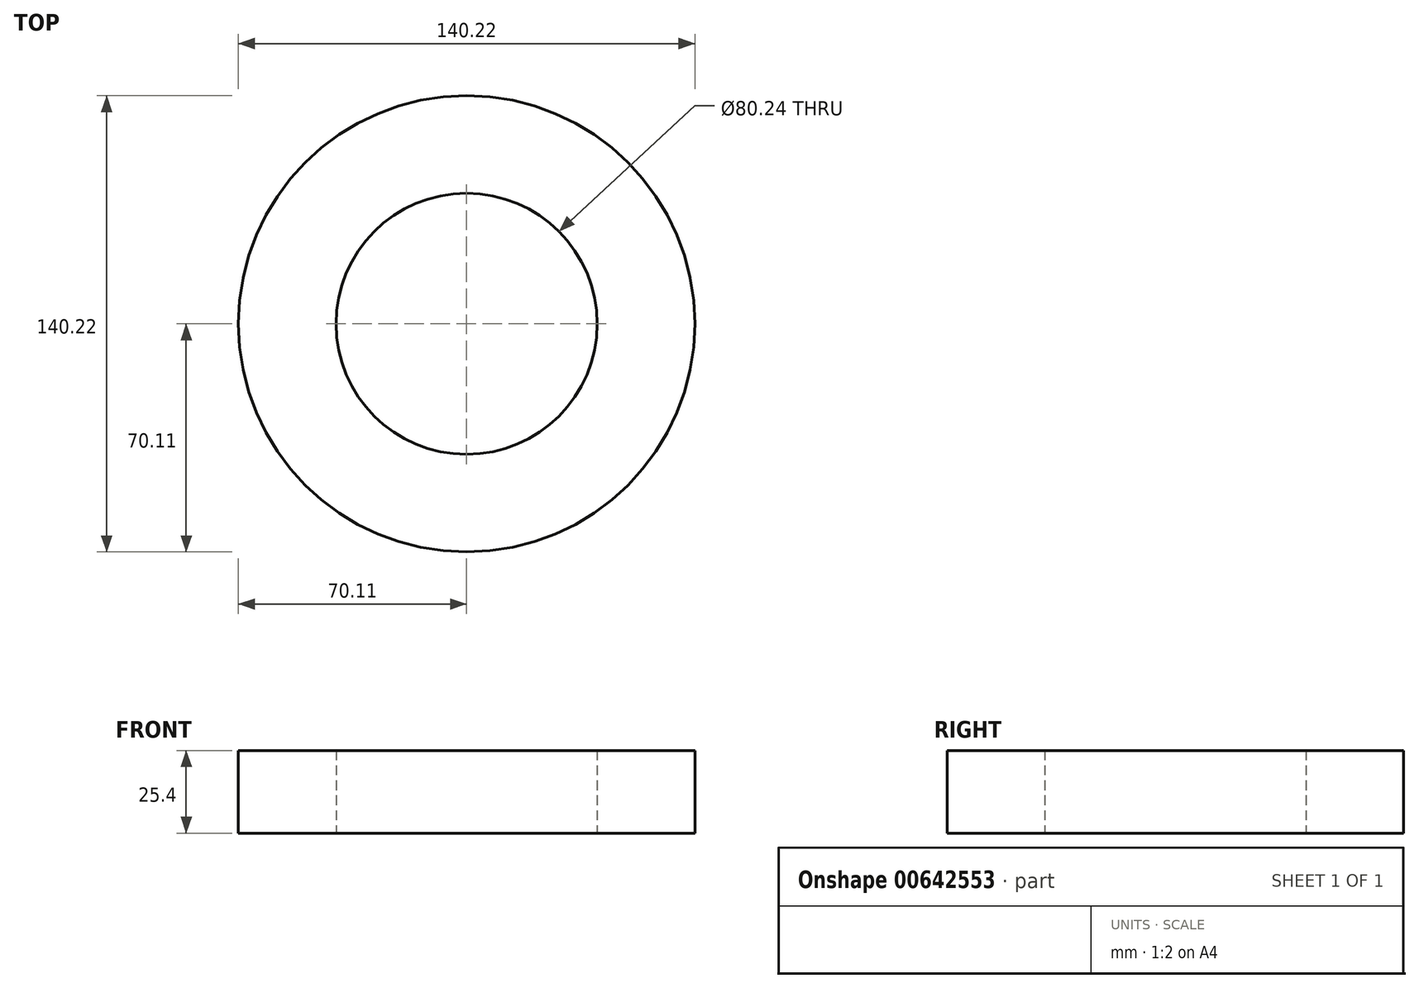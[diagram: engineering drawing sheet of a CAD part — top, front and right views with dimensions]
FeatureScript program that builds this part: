
annotation { "Feature Type Name" : "Feature", "Feature Type Description" : "" }
export const myFeature = defineFeature(function(context is Context, id is Id, definition is map)
    precondition{}
    {
        {
            var Q0;
            Q0=qCreatedBy(makeId("Top.planeOp"),FACE);
            var sketch = newSketch(context, id + "F0", { "sketchPlane" : qUnion([Q0])});
            skCircle(sketch, "E0", {"center": v(0, 0) * mm, "radius": 70.11 * mm});
            skCircle(sketch, "E1", {"center": v(0, 0) * mm, "radius": 40.12 * mm});
            skSolve(sketch);
        }
        {
            var Q0;
            Q0 = qSketchRegion(id + "F0", true);
            extrude(context, id + "F1", {"entities" : qUnion([Q0]), "depth" : 25.4 * mm, "offsetDistance" : 25.4 * mm});
        }
    });
